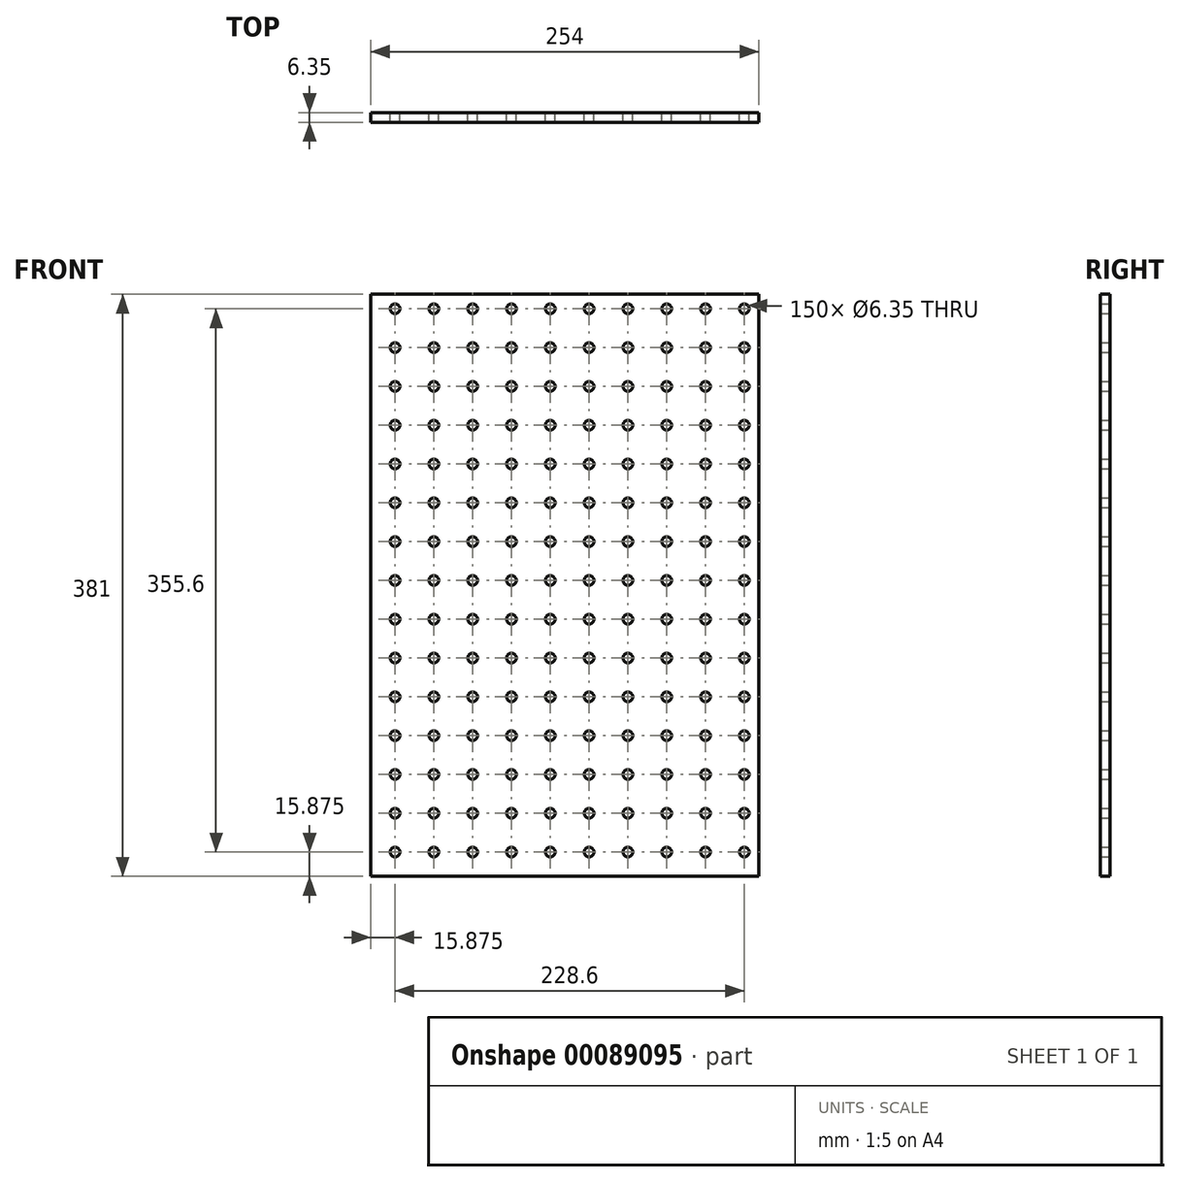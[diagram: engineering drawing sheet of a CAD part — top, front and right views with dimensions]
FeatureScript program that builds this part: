
annotation { "Feature Type Name" : "Feature", "Feature Type Description" : "" }
export const myFeature = defineFeature(function(context is Context, id is Id, definition is map)
    precondition{}
    {
        {
            var Q0;
            Q0=qCreatedBy(makeId("Front.planeOp"),FACE);
            var sketch = newSketch(context, id + "F0", { "sketchPlane" : qUnion([Q0])});
            skLineSegment(sketch, "E0.bottom", {"start": v(127, 190.5) * mm, "end": v(-127, 190.5) * mm});
            skLineSegment(sketch, "E0.top", {"start": v(127, -190.5) * mm, "end": v(-127, -190.5) * mm});
            skLineSegment(sketch, "E0.left", {"start": v(127, 190.5) * mm, "end": v(127, -190.5) * mm});
            skLineSegment(sketch, "E0.right", {"start": v(-127, 190.5) * mm, "end": v(-127, -190.5) * mm});
            skPoint(sketch, "E0.middle", {"position": v(0, 0) * mm});
            skSolve(sketch);
        }
        {
            var Q0;
            Q0=makeQuery(id+"F0.imprint","IMPRINT",FACE,{"disambiguationData":[TD([[makeQuery(id+"F0.imprint","IMPRINT",EDGE,{"derivedFrom":sQuery(id+"F0.wireOp",EDGE,"E0.bottom")}),1.0]])]});
            extrude(context, id + "F1", {"entities" : qUnion([Q0]), "depth" : 6.35 * mm});
        }
        {
            var Q0;
            Q0=makeQuery(id+"F1.opExtrude","CAP_FACE",FACE,{"disambiguationData":[OSD([sQuery(id+"F0.wireOp",EDGE,"E0.bottom"),sQuery(id+"F0.wireOp",EDGE,"E0.top"),sQuery(id+"F0.wireOp",EDGE,"E0.left"),sQuery(id+"F0.wireOp",EDGE,"E0.right")])],"isStart":true});
            var sketch = newSketch(context, id + "F2", { "sketchPlane" : qUnion([Q0])});
            skCircle(sketch, "E1", {"center": v(-117.47, 180.98) * mm, "radius": 3.18 * mm});
            skCircle(sketch, "E2.1.0.0", {"center": v(-92.07, 180.98) * mm, "radius": 3.18 * mm});
            skCircle(sketch, "E2.2.0.0", {"center": v(-66.67, 180.98) * mm, "radius": 3.18 * mm});
            skCircle(sketch, "E2.3.0.0", {"center": v(-41.27, 180.98) * mm, "radius": 3.18 * mm});
            skCircle(sketch, "E2.4.0.0", {"center": v(-15.87, 180.98) * mm, "radius": 3.18 * mm});
            skCircle(sketch, "E2.5.0.0", {"center": v(9.53, 180.98) * mm, "radius": 3.18 * mm});
            skCircle(sketch, "E2.6.0.0", {"center": v(34.93, 180.98) * mm, "radius": 3.18 * mm});
            skCircle(sketch, "E2.7.0.0", {"center": v(60.33, 180.98) * mm, "radius": 3.18 * mm});
            skCircle(sketch, "E2.8.0.0", {"center": v(85.73, 180.98) * mm, "radius": 3.18 * mm});
            skCircle(sketch, "E2.9.0.0", {"center": v(111.13, 180.98) * mm, "radius": 3.18 * mm});
            skLineSegment(sketch, "E2.direction1", {"start": v(-117.47, 180.98) * mm, "end": v(-92.07, 180.98) * mm, "construction": true});
            skCircle(sketch, "E3.0.1.0", {"center": v(111.13, 155.58) * mm, "radius": 3.18 * mm});
            skCircle(sketch, "E3.0.1.1", {"center": v(85.73, 155.58) * mm, "radius": 3.18 * mm});
            skCircle(sketch, "E3.0.1.2", {"center": v(60.33, 155.58) * mm, "radius": 3.18 * mm});
            skCircle(sketch, "E3.0.1.3", {"center": v(34.93, 155.58) * mm, "radius": 3.18 * mm});
            skCircle(sketch, "E3.0.1.4", {"center": v(9.53, 155.58) * mm, "radius": 3.18 * mm});
            skCircle(sketch, "E3.0.1.5", {"center": v(-15.87, 155.58) * mm, "radius": 3.18 * mm});
            skCircle(sketch, "E3.0.1.6", {"center": v(-41.27, 155.58) * mm, "radius": 3.18 * mm});
            skCircle(sketch, "E3.0.1.7", {"center": v(-66.67, 155.58) * mm, "radius": 3.18 * mm});
            skCircle(sketch, "E3.0.1.8", {"center": v(-92.07, 155.58) * mm, "radius": 3.18 * mm});
            skCircle(sketch, "E3.0.1.9", {"center": v(-117.47, 155.58) * mm, "radius": 3.18 * mm});
            skCircle(sketch, "E3.0.2.0", {"center": v(111.13, 130.18) * mm, "radius": 3.18 * mm});
            skCircle(sketch, "E3.0.2.1", {"center": v(85.73, 130.18) * mm, "radius": 3.18 * mm});
            skCircle(sketch, "E3.0.2.2", {"center": v(60.33, 130.18) * mm, "radius": 3.18 * mm});
            skCircle(sketch, "E3.0.2.3", {"center": v(34.93, 130.18) * mm, "radius": 3.18 * mm});
            skCircle(sketch, "E3.0.2.4", {"center": v(9.53, 130.18) * mm, "radius": 3.18 * mm});
            skCircle(sketch, "E3.0.2.5", {"center": v(-15.87, 130.18) * mm, "radius": 3.18 * mm});
            skCircle(sketch, "E3.0.2.6", {"center": v(-41.27, 130.18) * mm, "radius": 3.18 * mm});
            skCircle(sketch, "E3.0.2.7", {"center": v(-66.67, 130.18) * mm, "radius": 3.18 * mm});
            skCircle(sketch, "E3.0.2.8", {"center": v(-92.07, 130.18) * mm, "radius": 3.18 * mm});
            skCircle(sketch, "E3.0.2.9", {"center": v(-117.47, 130.18) * mm, "radius": 3.18 * mm});
            skCircle(sketch, "E3.0.3.0", {"center": v(111.13, 104.78) * mm, "radius": 3.18 * mm});
            skCircle(sketch, "E3.0.3.1", {"center": v(85.73, 104.78) * mm, "radius": 3.18 * mm});
            skCircle(sketch, "E3.0.3.2", {"center": v(60.33, 104.78) * mm, "radius": 3.18 * mm});
            skCircle(sketch, "E3.0.3.3", {"center": v(34.93, 104.78) * mm, "radius": 3.18 * mm});
            skCircle(sketch, "E3.0.3.4", {"center": v(9.53, 104.78) * mm, "radius": 3.18 * mm});
            skCircle(sketch, "E3.0.3.5", {"center": v(-15.87, 104.78) * mm, "radius": 3.18 * mm});
            skCircle(sketch, "E3.0.3.6", {"center": v(-41.27, 104.78) * mm, "radius": 3.18 * mm});
            skCircle(sketch, "E3.0.3.7", {"center": v(-66.67, 104.78) * mm, "radius": 3.18 * mm});
            skCircle(sketch, "E3.0.3.8", {"center": v(-92.07, 104.78) * mm, "radius": 3.18 * mm});
            skCircle(sketch, "E3.0.3.9", {"center": v(-117.47, 104.78) * mm, "radius": 3.18 * mm});
            skCircle(sketch, "E3.0.4.0", {"center": v(111.13, 79.38) * mm, "radius": 3.18 * mm});
            skCircle(sketch, "E3.0.4.1", {"center": v(85.73, 79.38) * mm, "radius": 3.18 * mm});
            skCircle(sketch, "E3.0.4.2", {"center": v(60.33, 79.38) * mm, "radius": 3.18 * mm});
            skCircle(sketch, "E3.0.4.3", {"center": v(34.93, 79.38) * mm, "radius": 3.18 * mm});
            skCircle(sketch, "E3.0.4.4", {"center": v(9.53, 79.38) * mm, "radius": 3.18 * mm});
            skCircle(sketch, "E3.0.4.5", {"center": v(-15.87, 79.38) * mm, "radius": 3.18 * mm});
            skCircle(sketch, "E3.0.4.6", {"center": v(-41.27, 79.38) * mm, "radius": 3.18 * mm});
            skCircle(sketch, "E3.0.4.7", {"center": v(-66.67, 79.38) * mm, "radius": 3.18 * mm});
            skCircle(sketch, "E3.0.4.8", {"center": v(-92.07, 79.38) * mm, "radius": 3.18 * mm});
            skCircle(sketch, "E3.0.4.9", {"center": v(-117.47, 79.38) * mm, "radius": 3.18 * mm});
            skCircle(sketch, "E3.0.5.0", {"center": v(111.13, 53.97) * mm, "radius": 3.18 * mm});
            skCircle(sketch, "E3.0.5.1", {"center": v(85.73, 53.97) * mm, "radius": 3.18 * mm});
            skCircle(sketch, "E3.0.5.2", {"center": v(60.33, 53.97) * mm, "radius": 3.18 * mm});
            skCircle(sketch, "E3.0.5.3", {"center": v(34.93, 53.97) * mm, "radius": 3.18 * mm});
            skCircle(sketch, "E3.0.5.4", {"center": v(9.53, 53.97) * mm, "radius": 3.18 * mm});
            skCircle(sketch, "E3.0.5.5", {"center": v(-15.87, 53.97) * mm, "radius": 3.18 * mm});
            skCircle(sketch, "E3.0.5.6", {"center": v(-41.27, 53.97) * mm, "radius": 3.18 * mm});
            skCircle(sketch, "E3.0.5.7", {"center": v(-66.67, 53.97) * mm, "radius": 3.18 * mm});
            skCircle(sketch, "E3.0.5.8", {"center": v(-92.07, 53.97) * mm, "radius": 3.18 * mm});
            skCircle(sketch, "E3.0.5.9", {"center": v(-117.47, 53.97) * mm, "radius": 3.18 * mm});
            skCircle(sketch, "E3.0.6.0", {"center": v(111.13, 28.57) * mm, "radius": 3.18 * mm});
            skCircle(sketch, "E3.0.6.1", {"center": v(85.73, 28.57) * mm, "radius": 3.18 * mm});
            skCircle(sketch, "E3.0.6.2", {"center": v(60.33, 28.57) * mm, "radius": 3.18 * mm});
            skCircle(sketch, "E3.0.6.3", {"center": v(34.93, 28.57) * mm, "radius": 3.18 * mm});
            skCircle(sketch, "E3.0.6.4", {"center": v(9.53, 28.57) * mm, "radius": 3.18 * mm});
            skCircle(sketch, "E3.0.6.5", {"center": v(-15.87, 28.57) * mm, "radius": 3.18 * mm});
            skCircle(sketch, "E3.0.6.6", {"center": v(-41.27, 28.57) * mm, "radius": 3.18 * mm});
            skCircle(sketch, "E3.0.6.7", {"center": v(-66.67, 28.57) * mm, "radius": 3.18 * mm});
            skCircle(sketch, "E3.0.6.8", {"center": v(-92.07, 28.57) * mm, "radius": 3.18 * mm});
            skCircle(sketch, "E3.0.6.9", {"center": v(-117.47, 28.57) * mm, "radius": 3.18 * mm});
            skCircle(sketch, "E3.0.7.0", {"center": v(111.13, 3.17) * mm, "radius": 3.18 * mm});
            skCircle(sketch, "E3.0.7.1", {"center": v(85.73, 3.17) * mm, "radius": 3.18 * mm});
            skCircle(sketch, "E3.0.7.2", {"center": v(60.33, 3.17) * mm, "radius": 3.18 * mm});
            skCircle(sketch, "E3.0.7.3", {"center": v(34.93, 3.17) * mm, "radius": 3.18 * mm});
            skCircle(sketch, "E3.0.7.4", {"center": v(9.53, 3.17) * mm, "radius": 3.18 * mm});
            skCircle(sketch, "E3.0.7.5", {"center": v(-15.87, 3.17) * mm, "radius": 3.18 * mm});
            skCircle(sketch, "E3.0.7.6", {"center": v(-41.27, 3.17) * mm, "radius": 3.18 * mm});
            skCircle(sketch, "E3.0.7.7", {"center": v(-66.67, 3.17) * mm, "radius": 3.18 * mm});
            skCircle(sketch, "E3.0.7.8", {"center": v(-92.07, 3.17) * mm, "radius": 3.18 * mm});
            skCircle(sketch, "E3.0.7.9", {"center": v(-117.47, 3.17) * mm, "radius": 3.18 * mm});
            skCircle(sketch, "E3.0.8.0", {"center": v(111.13, -22.23) * mm, "radius": 3.18 * mm});
            skCircle(sketch, "E3.0.8.1", {"center": v(85.73, -22.23) * mm, "radius": 3.18 * mm});
            skCircle(sketch, "E3.0.8.2", {"center": v(60.33, -22.23) * mm, "radius": 3.18 * mm});
            skCircle(sketch, "E3.0.8.3", {"center": v(34.93, -22.23) * mm, "radius": 3.18 * mm});
            skCircle(sketch, "E3.0.8.4", {"center": v(9.53, -22.23) * mm, "radius": 3.18 * mm});
            skCircle(sketch, "E3.0.8.5", {"center": v(-15.87, -22.23) * mm, "radius": 3.18 * mm});
            skCircle(sketch, "E3.0.8.6", {"center": v(-41.27, -22.23) * mm, "radius": 3.18 * mm});
            skCircle(sketch, "E3.0.8.7", {"center": v(-66.67, -22.23) * mm, "radius": 3.18 * mm});
            skCircle(sketch, "E3.0.8.8", {"center": v(-92.07, -22.23) * mm, "radius": 3.18 * mm});
            skCircle(sketch, "E3.0.8.9", {"center": v(-117.47, -22.23) * mm, "radius": 3.18 * mm});
            skCircle(sketch, "E3.0.9.0", {"center": v(111.13, -47.63) * mm, "radius": 3.18 * mm});
            skCircle(sketch, "E3.0.9.1", {"center": v(85.73, -47.63) * mm, "radius": 3.18 * mm});
            skCircle(sketch, "E3.0.9.2", {"center": v(60.33, -47.63) * mm, "radius": 3.18 * mm});
            skCircle(sketch, "E3.0.9.3", {"center": v(34.93, -47.63) * mm, "radius": 3.18 * mm});
            skCircle(sketch, "E3.0.9.4", {"center": v(9.53, -47.63) * mm, "radius": 3.18 * mm});
            skCircle(sketch, "E3.0.9.5", {"center": v(-15.87, -47.63) * mm, "radius": 3.18 * mm});
            skCircle(sketch, "E3.0.9.6", {"center": v(-41.27, -47.63) * mm, "radius": 3.18 * mm});
            skCircle(sketch, "E3.0.9.7", {"center": v(-66.67, -47.63) * mm, "radius": 3.18 * mm});
            skCircle(sketch, "E3.0.9.8", {"center": v(-92.07, -47.63) * mm, "radius": 3.18 * mm});
            skCircle(sketch, "E3.0.9.9", {"center": v(-117.47, -47.63) * mm, "radius": 3.18 * mm});
            skCircle(sketch, "E3.0.10.0", {"center": v(111.13, -73.03) * mm, "radius": 3.18 * mm});
            skCircle(sketch, "E3.0.10.1", {"center": v(85.73, -73.03) * mm, "radius": 3.18 * mm});
            skCircle(sketch, "E3.0.10.2", {"center": v(60.33, -73.03) * mm, "radius": 3.18 * mm});
            skCircle(sketch, "E3.0.10.3", {"center": v(34.93, -73.03) * mm, "radius": 3.18 * mm});
            skCircle(sketch, "E3.0.10.4", {"center": v(9.53, -73.03) * mm, "radius": 3.18 * mm});
            skCircle(sketch, "E3.0.10.5", {"center": v(-15.87, -73.03) * mm, "radius": 3.18 * mm});
            skCircle(sketch, "E3.0.10.6", {"center": v(-41.27, -73.03) * mm, "radius": 3.18 * mm});
            skCircle(sketch, "E3.0.10.7", {"center": v(-66.67, -73.03) * mm, "radius": 3.18 * mm});
            skCircle(sketch, "E3.0.10.8", {"center": v(-92.07, -73.03) * mm, "radius": 3.18 * mm});
            skCircle(sketch, "E3.0.10.9", {"center": v(-117.47, -73.03) * mm, "radius": 3.18 * mm});
            skCircle(sketch, "E3.0.11.0", {"center": v(111.13, -98.43) * mm, "radius": 3.18 * mm});
            skCircle(sketch, "E3.0.11.1", {"center": v(85.73, -98.43) * mm, "radius": 3.18 * mm});
            skCircle(sketch, "E3.0.11.2", {"center": v(60.33, -98.43) * mm, "radius": 3.18 * mm});
            skCircle(sketch, "E3.0.11.3", {"center": v(34.93, -98.43) * mm, "radius": 3.18 * mm});
            skCircle(sketch, "E3.0.11.4", {"center": v(9.53, -98.43) * mm, "radius": 3.18 * mm});
            skCircle(sketch, "E3.0.11.5", {"center": v(-15.87, -98.43) * mm, "radius": 3.18 * mm});
            skCircle(sketch, "E3.0.11.6", {"center": v(-41.27, -98.43) * mm, "radius": 3.18 * mm});
            skCircle(sketch, "E3.0.11.7", {"center": v(-66.67, -98.43) * mm, "radius": 3.18 * mm});
            skCircle(sketch, "E3.0.11.8", {"center": v(-92.07, -98.43) * mm, "radius": 3.18 * mm});
            skCircle(sketch, "E3.0.11.9", {"center": v(-117.47, -98.43) * mm, "radius": 3.18 * mm});
            skCircle(sketch, "E3.0.12.0", {"center": v(111.13, -123.83) * mm, "radius": 3.18 * mm});
            skCircle(sketch, "E3.0.12.1", {"center": v(85.73, -123.83) * mm, "radius": 3.18 * mm});
            skCircle(sketch, "E3.0.12.2", {"center": v(60.33, -123.83) * mm, "radius": 3.18 * mm});
            skCircle(sketch, "E3.0.12.3", {"center": v(34.93, -123.83) * mm, "radius": 3.18 * mm});
            skCircle(sketch, "E3.0.12.4", {"center": v(9.53, -123.83) * mm, "radius": 3.18 * mm});
            skCircle(sketch, "E3.0.12.5", {"center": v(-15.87, -123.83) * mm, "radius": 3.18 * mm});
            skCircle(sketch, "E3.0.12.6", {"center": v(-41.27, -123.83) * mm, "radius": 3.18 * mm});
            skCircle(sketch, "E3.0.12.7", {"center": v(-66.67, -123.83) * mm, "radius": 3.18 * mm});
            skCircle(sketch, "E3.0.12.8", {"center": v(-92.07, -123.83) * mm, "radius": 3.18 * mm});
            skCircle(sketch, "E3.0.12.9", {"center": v(-117.47, -123.83) * mm, "radius": 3.18 * mm});
            skCircle(sketch, "E3.0.13.0", {"center": v(111.13, -149.23) * mm, "radius": 3.18 * mm});
            skCircle(sketch, "E3.0.13.1", {"center": v(85.73, -149.23) * mm, "radius": 3.18 * mm});
            skCircle(sketch, "E3.0.13.2", {"center": v(60.33, -149.23) * mm, "radius": 3.18 * mm});
            skCircle(sketch, "E3.0.13.3", {"center": v(34.93, -149.23) * mm, "radius": 3.18 * mm});
            skCircle(sketch, "E3.0.13.4", {"center": v(9.53, -149.23) * mm, "radius": 3.18 * mm});
            skCircle(sketch, "E3.0.13.5", {"center": v(-15.87, -149.23) * mm, "radius": 3.18 * mm});
            skCircle(sketch, "E3.0.13.6", {"center": v(-41.27, -149.23) * mm, "radius": 3.18 * mm});
            skCircle(sketch, "E3.0.13.7", {"center": v(-66.67, -149.23) * mm, "radius": 3.18 * mm});
            skCircle(sketch, "E3.0.13.8", {"center": v(-92.07, -149.23) * mm, "radius": 3.18 * mm});
            skCircle(sketch, "E3.0.13.9", {"center": v(-117.47, -149.23) * mm, "radius": 3.18 * mm});
            skCircle(sketch, "E3.0.14.0", {"center": v(111.13, -174.63) * mm, "radius": 3.18 * mm});
            skCircle(sketch, "E3.0.14.1", {"center": v(85.73, -174.63) * mm, "radius": 3.18 * mm});
            skCircle(sketch, "E3.0.14.2", {"center": v(60.33, -174.63) * mm, "radius": 3.18 * mm});
            skCircle(sketch, "E3.0.14.3", {"center": v(34.93, -174.63) * mm, "radius": 3.18 * mm});
            skCircle(sketch, "E3.0.14.4", {"center": v(9.53, -174.63) * mm, "radius": 3.18 * mm});
            skCircle(sketch, "E3.0.14.5", {"center": v(-15.87, -174.63) * mm, "radius": 3.18 * mm});
            skCircle(sketch, "E3.0.14.6", {"center": v(-41.27, -174.63) * mm, "radius": 3.18 * mm});
            skCircle(sketch, "E3.0.14.7", {"center": v(-66.67, -174.63) * mm, "radius": 3.18 * mm});
            skCircle(sketch, "E3.0.14.8", {"center": v(-92.07, -174.63) * mm, "radius": 3.18 * mm});
            skCircle(sketch, "E3.0.14.9", {"center": v(-117.47, -174.63) * mm, "radius": 3.18 * mm});
            skLineSegment(sketch, "E3.direction1", {"start": v(111.13, 180.98) * mm, "end": v(136.53, 180.98) * mm, "construction": true});
            skLineSegment(sketch, "E3.direction2", {"start": v(111.13, 180.98) * mm, "end": v(111.13, 155.58) * mm, "construction": true});
            skSolve(sketch);
        }
        {
            var Q0;
            Q0 = qSketchRegion(id + "F2", true);
            extrude(context, id + "F3", {"entities" : qUnion([Q0]), "operationType" : NewBodyOperationType.REMOVE, "endBound" : BoundingType.UP_TO_NEXT, "oppositeDirection" : true, "depth" : 25.4 * mm});
        }
    });
